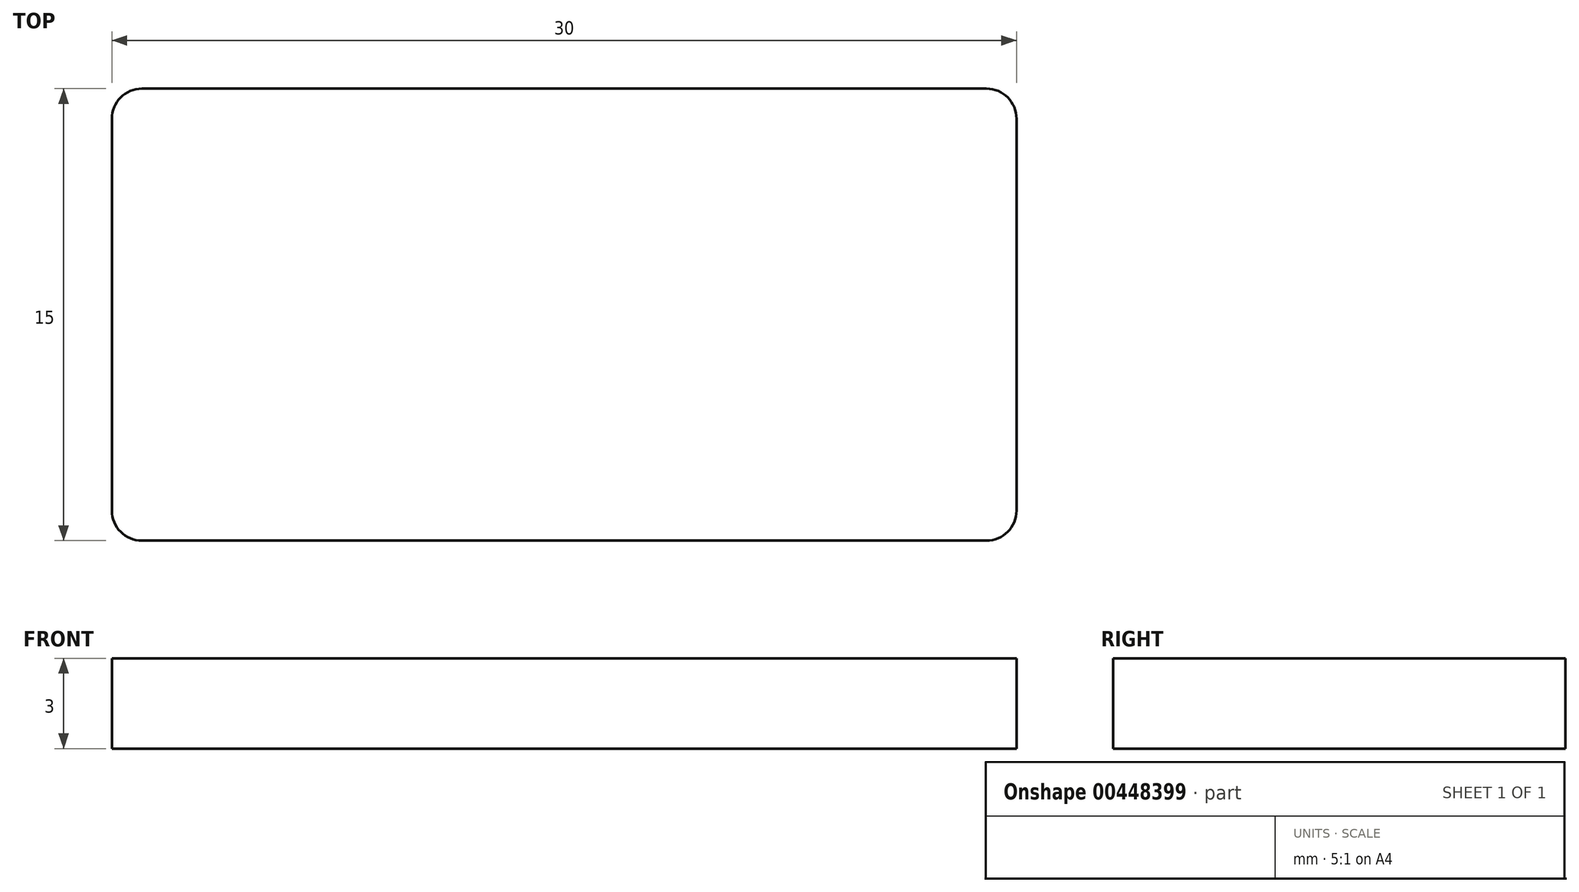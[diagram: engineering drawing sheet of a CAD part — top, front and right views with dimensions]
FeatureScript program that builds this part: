
annotation { "Feature Type Name" : "Feature", "Feature Type Description" : "" }
export const myFeature = defineFeature(function(context is Context, id is Id, definition is map)
    precondition{}
    {
        {
            var Q0;
            Q0=qCreatedBy(makeId("Top.planeOp"),FACE);
            var sketch = newSketch(context, id + "F0", { "sketchPlane" : qUnion([Q0])});
            skLineSegment(sketch, "E0.bottom", {"start": v(15, 7.5) * mm, "end": v(-15, 7.5) * mm});
            skLineSegment(sketch, "E0.top", {"start": v(15, -7.5) * mm, "end": v(-15, -7.5) * mm});
            skLineSegment(sketch, "E0.left", {"start": v(15, 7.5) * mm, "end": v(15, -7.5) * mm});
            skLineSegment(sketch, "E0.right", {"start": v(-15, 7.5) * mm, "end": v(-15, -7.5) * mm});
            skPoint(sketch, "E0.middle", {"position": v(0, 0) * mm});
            skSolve(sketch);
        }
        {
            var Q0;
            Q0 = qSketchRegion(id + "F0", true);
            extrude(context, id + "F1", {"entities" : qUnion([Q0]), "depth" : 3 * mm});
        }
        {
            var Q0;
            Q0=makeQuery(id+"F1.opExtrude","SWEPT_EDGE",EDGE,{"disambiguationData":[OSD([sQuery(id+"F0.wireOp",EDGE,"E0.bottom"),sQuery(id+"F0.wireOp",EDGE,"E0.left")])]});
            var Q1;
            Q1=makeQuery(id+"F1.opExtrude","SWEPT_EDGE",EDGE,{"disambiguationData":[OSD([sQuery(id+"F0.wireOp",EDGE,"E0.top"),sQuery(id+"F0.wireOp",EDGE,"E0.left")])]});
            var Q2;
            Q2=makeQuery(id+"F1.opExtrude","SWEPT_EDGE",EDGE,{"disambiguationData":[OSD([sQuery(id+"F0.wireOp",EDGE,"E0.bottom"),sQuery(id+"F0.wireOp",EDGE,"E0.right")])]});
            var Q3;
            Q3=makeQuery(id+"F1.opExtrude","SWEPT_EDGE",EDGE,{"disambiguationData":[OSD([sQuery(id+"F0.wireOp",EDGE,"E0.top"),sQuery(id+"F0.wireOp",EDGE,"E0.right")])]});
            fillet(context, id + "F2", {"entities" : qUnion([Q0, Q1, Q2, Q3]), "radius" : 1 * mm, "tangentPropagation" : true, "allowEdgeOverflow" : false});
        }
    });
